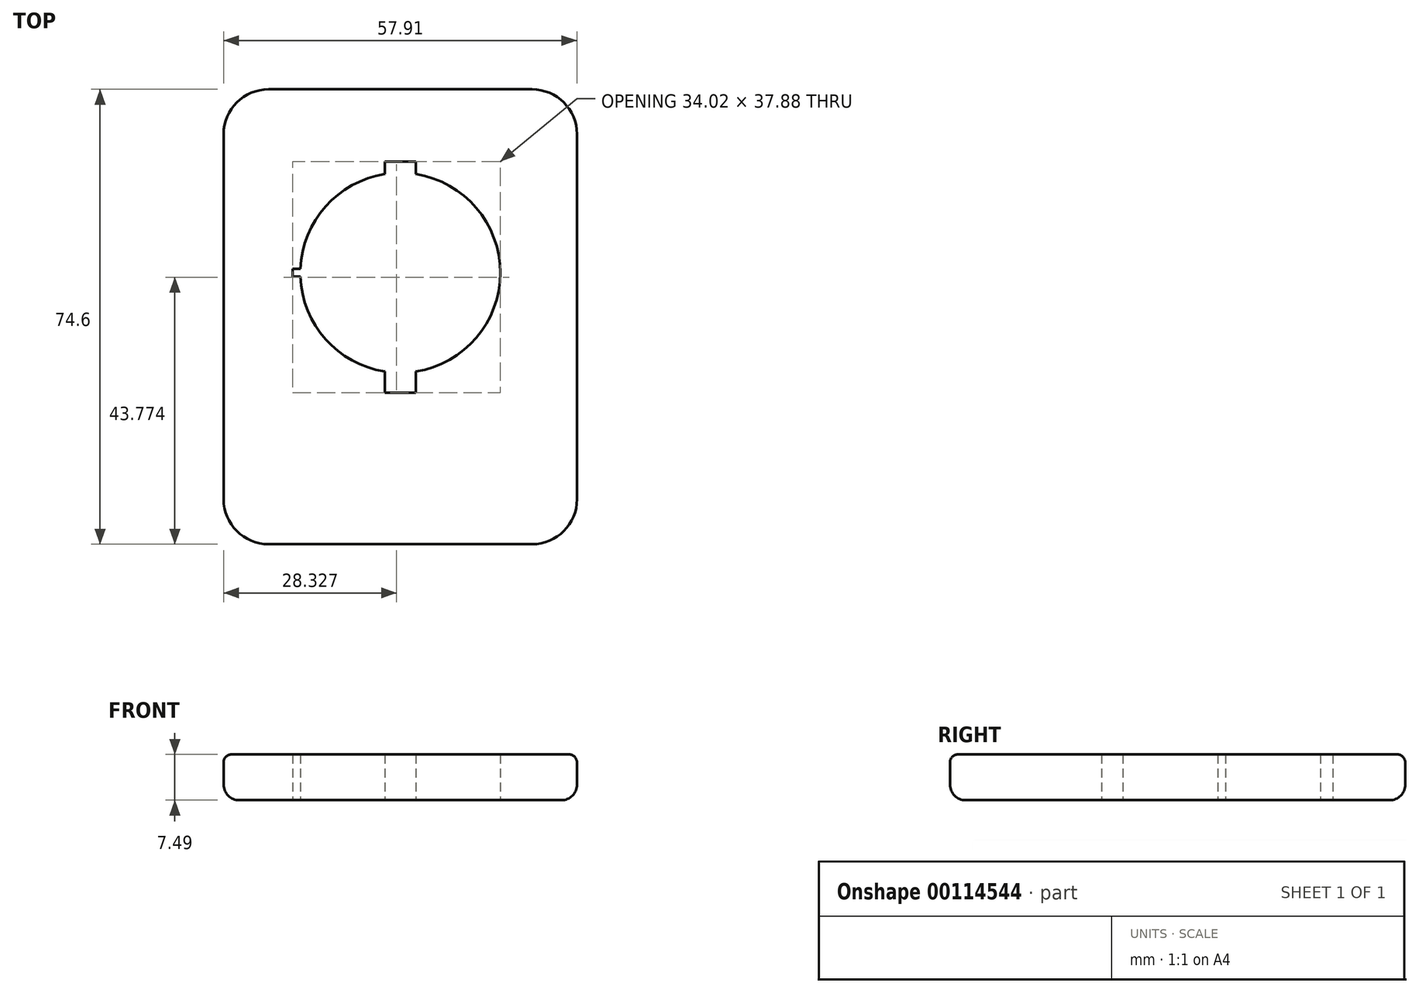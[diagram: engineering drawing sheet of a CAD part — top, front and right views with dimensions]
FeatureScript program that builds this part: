
annotation { "Feature Type Name" : "Feature", "Feature Type Description" : "" }
export const myFeature = defineFeature(function(context is Context, id is Id, definition is map)
    precondition{}
    {
        {
            var Q0;
            Q0=qCreatedBy(makeId("Top.planeOp"),FACE);
            var sketch = newSketch(context, id + "F0", { "sketchPlane" : qUnion([Q0])});
            skLineSegment(sketch, "E0.bottom", {"start": v(-8.66, -24.68) * mm, "end": v(49.25, -24.68) * mm});
            skLineSegment(sketch, "E0.top", {"start": v(-8.66, 49.92) * mm, "end": v(49.25, 49.92) * mm});
            skLineSegment(sketch, "E0.left", {"start": v(-8.66, -24.68) * mm, "end": v(-8.66, 49.92) * mm});
            skLineSegment(sketch, "E0.right", {"start": v(49.25, -24.68) * mm, "end": v(49.25, 49.92) * mm});
            skArc(sketch, "E1", {"start": v(3.93, 19.18) * mm, "mid": v(8.05, 8.93) * mm, "end": v(17.76, 3.63) * mm});
            skLineSegment(sketch, "E2", {"start": v(3.93, 19.18) * mm, "end": v(2.66, 19.18) * mm});
            skLineSegment(sketch, "E3", {"start": v(2.66, 19.18) * mm, "end": v(2.66, 20.45) * mm});
            skLineSegment(sketch, "E4", {"start": v(2.66, 20.45) * mm, "end": v(3.93, 20.45) * mm});
            skLineSegment(sketch, "E5", {"start": v(17.76, 3.63) * mm, "end": v(17.76, 0.15) * mm});
            skLineSegment(sketch, "E6", {"start": v(17.76, 0.15) * mm, "end": v(22.84, 0.15) * mm});
            skLineSegment(sketch, "E7", {"start": v(22.84, 0.15) * mm, "end": v(22.84, 3.63) * mm});
            skLineSegment(sketch, "E8", {"start": v(17.76, 36) * mm, "end": v(17.76, 38.03) * mm});
            skLineSegment(sketch, "E9", {"start": v(17.76, 38.03) * mm, "end": v(22.84, 38.03) * mm});
            skLineSegment(sketch, "E10", {"start": v(22.84, 38.03) * mm, "end": v(22.84, 36) * mm});
            skArc(sketch, "E11.trimOffspring", {"start": v(22.84, 3.63) * mm, "mid": v(36.68, 19.82) * mm, "end": v(22.84, 36) * mm});
            skArc(sketch, "E12.trimOffspring", {"start": v(17.76, 36) * mm, "mid": v(8.05, 30.7) * mm, "end": v(3.93, 20.45) * mm});
            skSolve(sketch);
        }
        {
            var Q0;
            Q0=makeQuery(id+"F0.imprint","IMPRINT",FACE,{"disambiguationData":[TD([[makeQuery(id+"F0.imprint","IMPRINT",EDGE,{"derivedFrom":sQuery(id+"F0.wireOp",EDGE,"E0.bottom")}),1.0]])]});
            extrude(context, id + "F1", {"entities" : qUnion([Q0]), "depth" : 7.5 * mm});
        }
        {
            var Q0;
            Q0=makeQuery(id+"F1.opExtrude","SWEPT_EDGE",EDGE,{"disambiguationData":[OSD([sQuery(id+"F0.wireOp",EDGE,"E0.bottom"),sQuery(id+"F0.wireOp",EDGE,"E0.left")])]});
            var Q1;
            Q1=makeQuery(id+"F1.opExtrude","SWEPT_EDGE",EDGE,{"disambiguationData":[OSD([sQuery(id+"F0.wireOp",EDGE,"E0.bottom"),sQuery(id+"F0.wireOp",EDGE,"E0.right")])]});
            var Q2;
            Q2=makeQuery(id+"F1.opExtrude","SWEPT_EDGE",EDGE,{"disambiguationData":[OSD([sQuery(id+"F0.wireOp",EDGE,"E0.top"),sQuery(id+"F0.wireOp",EDGE,"E0.right")])]});
            var Q3;
            Q3=makeQuery(id+"F1.opExtrude","SWEPT_EDGE",EDGE,{"disambiguationData":[OSD([sQuery(id+"F0.wireOp",EDGE,"E0.top"),sQuery(id+"F0.wireOp",EDGE,"E0.left")])]});
            fillet(context, id + "F2", {"entities" : qUnion([Q0, Q1, Q2, Q3]), "radius" : 7.37 * mm, "tangentPropagation" : true, "allowEdgeOverflow" : false});
        }
        {
            var Q0;
            Q0=makeQuery(id+"F1.opExtrude","CAP_EDGE",EDGE,{"disambiguationData":[OSD([sQuery(id+"F0.wireOp",EDGE,"E0.left")])],"isStart":false});
            fillet(context, id + "F3", {"entities" : qUnion([Q0]), "radius" : 1.27 * mm, "tangentPropagation" : true, "allowEdgeOverflow" : false});
        }
        {
            var Q0;
            Q0=makeQuery(id+"F1.opExtrude","CAP_EDGE",EDGE,{"disambiguationData":[OSD([sQuery(id+"F0.wireOp",EDGE,"E0.left")])],"isStart":true});
            fillet(context, id + "F4", {"entities" : qUnion([Q0]), "radius" : 2.54 * mm, "tangentPropagation" : true, "allowEdgeOverflow" : false});
        }
    });
